AUTODESK INVENTOR PART (.ipt)
format: ipt  version: 2022 (Build 260153000, 153)  size: 127,488 bytes
history: native  units: in
note: dims shown in document units (in); Inventor stores cm internally (conversion verified against a paired STEP export)
features: sketch x4, extrude x3, plane x1
ambient origin geometry x8: Origin, YZ Plane, XZ Plane, XY Plane, X Axis, Y Axis, Z Axis, Center Point
bodies: Solid1 (feature_tree)
feature tree (8):
  extrude  "Extrusion1"  Depth=0.9843in
  plane  "Work Plane2"
  extrude  "Extrusion3"  Depth=0.748in
  extrude  "Extrusion4"  Depth=0.0787in
  sketch  "Sketch5"  dims[d11=0.0787in d12=0.0787in d13=0.2362in d14=0.0in d15=0.8957in d16=0.1575in d17=0.8957in d18=0.0197in d19=0.0in d20=0.4921in d21=0.7874in]
  sketch  "Sketch1"  dims[d0=2.9921in d1=0.9843in]
  sketch  "Sketch3"  dims[d2=0.0984in d3=0.0in d8=0.748in]
  sketch  "Sketch4"  dims[d9=0.0787in d10=0.0787in]
